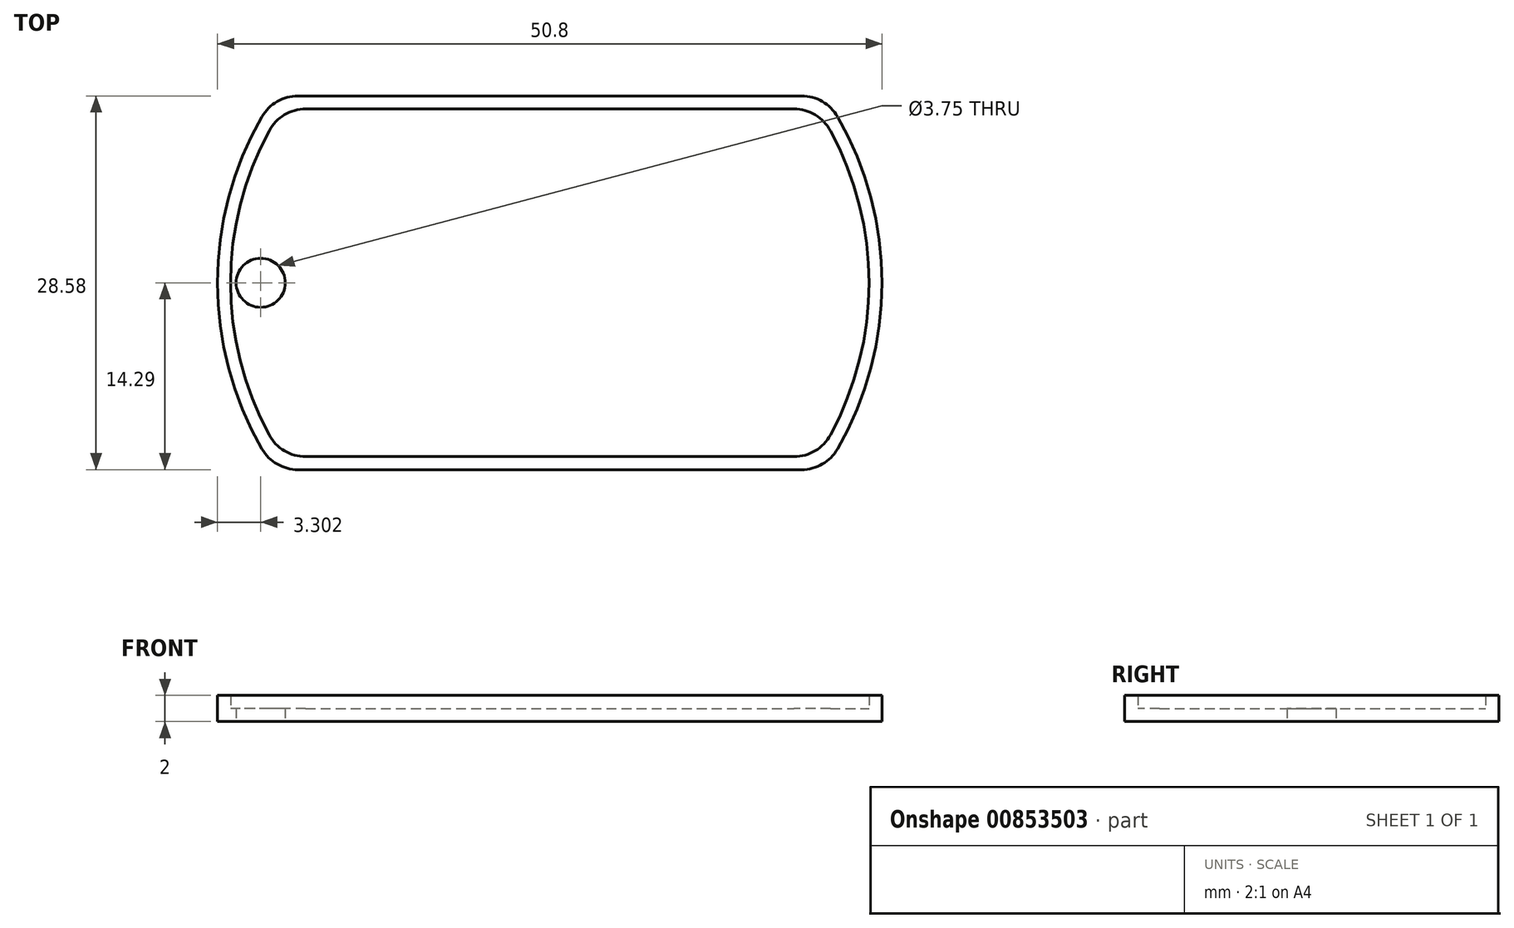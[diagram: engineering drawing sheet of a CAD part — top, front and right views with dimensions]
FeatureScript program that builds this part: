
annotation { "Feature Type Name" : "Feature", "Feature Type Description" : "" }
export const myFeature = defineFeature(function(context is Context, id is Id, definition is map)
    precondition{}
    {
        {
            var Q0;
            Q0=qCreatedBy(makeId("Top.planeOp"),FACE);
            var sketch = newSketch(context, id + "F0", { "sketchPlane" : qUnion([Q0])});
            skArc(sketch, "E0", {"start": v(-22, 12.7) * mm, "mid": v(-25.4, 0) * mm, "end": v(-22, -12.7) * mm});
            skLineSegment(sketch, "E1.top", {"start": v(-19.25, -14.29) * mm, "end": v(19.25, -14.29) * mm});
            skArc(sketch, "E2.trimOffspring", {"start": v(22, -12.7) * mm, "mid": v(25.4, 0) * mm, "end": v(22, 12.7) * mm});
            skLineSegment(sketch, "E3", {"start": v(-19.25, 14.29) * mm, "end": v(19.25, 14.29) * mm});
            skPoint(sketch, "E4.visualSharp", {"position": v(-21, 14.29) * mm});
            skArc(sketch, "E4.filletArc", {"start": v(-19.25, 14.29) * mm, "mid": v(-20.83, 13.86) * mm, "end": v(-22, 12.7) * mm});
            skPoint(sketch, "E5.visualSharp", {"position": v(21, 14.29) * mm});
            skArc(sketch, "E5.filletArc", {"start": v(22, 12.7) * mm, "mid": v(20.83, 13.86) * mm, "end": v(19.25, 14.29) * mm});
            skPoint(sketch, "E6.visualSharp", {"position": v(21, -14.29) * mm});
            skArc(sketch, "E6.filletArc", {"start": v(19.25, -14.29) * mm, "mid": v(20.83, -13.86) * mm, "end": v(22, -12.7) * mm});
            skPoint(sketch, "E7.visualSharp", {"position": v(-21, -14.29) * mm});
            skArc(sketch, "E7.filletArc", {"start": v(-22, -12.7) * mm, "mid": v(-20.83, -13.86) * mm, "end": v(-19.25, -14.29) * mm});
            skCircle(sketch, "E8", {"center": v(-22.1, 0) * mm, "radius": 1.87 * mm});
            skSolve(sketch);
        }
        {
            var Q0;
            Q0=makeQuery(id+"F0.imprint","IMPRINT",FACE,{"disambiguationData":[TD([[makeQuery(id+"F0.imprint","IMPRINT",EDGE,{"derivedFrom":sQuery(id+"F0.wireOp",EDGE,"E0")}),1.0]])]});
            extrude(context, id + "F1", {"entities" : qUnion([Q0]), "depth" : 1 * mm, "offsetDistance" : 25.4 * mm});
        }
        {
            var Q0;
            Q0=makeQuery(id+"F1.opExtrude","CAP_FACE",FACE,{"disambiguationData":[OSD([sQuery(id+"F0.wireOp",EDGE,"E0"),sQuery(id+"F0.wireOp",EDGE,"E1.top"),sQuery(id+"F0.wireOp",EDGE,"E2.trimOffspring"),sQuery(id+"F0.wireOp",EDGE,"E3"),sQuery(id+"F0.wireOp",EDGE,"E4.filletArc"),sQuery(id+"F0.wireOp",EDGE,"E5.filletArc"),sQuery(id+"F0.wireOp",EDGE,"E6.filletArc"),sQuery(id+"F0.wireOp",EDGE,"E7.filletArc")])],"isStart":false});
            var sketch = newSketch(context, id + "F2", { "sketchPlane" : qUnion([Q0])});
            skLineSegment(sketch, "E9.0", {"start": v(-18.66, 13.29) * mm, "end": v(18.66, 13.29) * mm});
            skArc(sketch, "E9.1", {"start": v(-21.45, 11.63) * mm, "mid": v(-24.4, 0) * mm, "end": v(-21.45, -11.63) * mm});
            skLineSegment(sketch, "E9.2", {"start": v(-18.66, -13.29) * mm, "end": v(18.66, -13.29) * mm});
            skArc(sketch, "E9.3", {"start": v(21.45, -11.63) * mm, "mid": v(24.4, 0) * mm, "end": v(21.45, 11.63) * mm});
            skPoint(sketch, "E10.visualSharp", {"position": v(-20.46, 13.29) * mm});
            skArc(sketch, "E10.filletArc", {"start": v(-18.66, 13.29) * mm, "mid": v(-20.29, 12.84) * mm, "end": v(-21.45, 11.63) * mm});
            skPoint(sketch, "E11.visualSharp", {"position": v(20.46, 13.29) * mm});
            skArc(sketch, "E11.filletArc", {"start": v(21.45, 11.63) * mm, "mid": v(20.29, 12.84) * mm, "end": v(18.66, 13.29) * mm});
            skPoint(sketch, "E12.visualSharp", {"position": v(20.46, -13.29) * mm});
            skArc(sketch, "E12.filletArc", {"start": v(18.66, -13.29) * mm, "mid": v(20.29, -12.84) * mm, "end": v(21.45, -11.63) * mm});
            skPoint(sketch, "E13.visualSharp", {"position": v(-20.46, -13.29) * mm});
            skArc(sketch, "E13.filletArc", {"start": v(-21.45, -11.63) * mm, "mid": v(-20.29, -12.84) * mm, "end": v(-18.66, -13.29) * mm});
            skLineSegment(sketch, "E14.0", {"start": v(-19.25, 14.29) * mm, "end": v(19.25, 14.29) * mm});
            skArc(sketch, "E14.1", {"start": v(-22, 12.7) * mm, "mid": v(-25.4, 0) * mm, "end": v(-22, -12.7) * mm});
            skLineSegment(sketch, "E14.2", {"start": v(-19.25, -14.29) * mm, "end": v(19.25, -14.29) * mm});
            skArc(sketch, "E14.3", {"start": v(22, -12.7) * mm, "mid": v(25.4, 0) * mm, "end": v(22, 12.7) * mm});
            skPoint(sketch, "E15.visualSharp", {"position": v(-21, -14.29) * mm});
            skArc(sketch, "E15.filletArc", {"start": v(-22, -12.7) * mm, "mid": v(-20.83, -13.86) * mm, "end": v(-19.25, -14.29) * mm});
            skPoint(sketch, "E16.visualSharp", {"position": v(21, -14.29) * mm});
            skArc(sketch, "E16.filletArc", {"start": v(19.25, -14.29) * mm, "mid": v(20.83, -13.86) * mm, "end": v(22, -12.7) * mm});
            skPoint(sketch, "E17.visualSharp", {"position": v(21, 14.29) * mm});
            skArc(sketch, "E17.filletArc", {"start": v(22, 12.7) * mm, "mid": v(20.83, 13.86) * mm, "end": v(19.25, 14.29) * mm});
            skPoint(sketch, "E18.visualSharp", {"position": v(-21, 14.29) * mm});
            skArc(sketch, "E18.filletArc", {"start": v(-19.25, 14.29) * mm, "mid": v(-20.83, 13.86) * mm, "end": v(-22, 12.7) * mm});
            skSolve(sketch);
        }
        {
            var Q0;
            Q0=makeQuery(id+"F2.imprint","IMPRINT",FACE,{"disambiguationData":[TD([[makeQuery(id+"F2.imprint","IMPRINT",EDGE,{"derivedFrom":sQuery(id+"F2.wireOp",EDGE,"E9.0")}),1.0]])]});
            extrude(context, id + "F3", {"entities" : qUnion([Q0]), "operationType" : NewBodyOperationType.ADD, "depth" : 1 * mm, "offsetDistance" : 25.4 * mm});
        }
        {
            var Q0;
            Q0=makeQuery(id+"F1.opExtrude","CAP_FACE",FACE,{"disambiguationData":[OSD([sQuery(id+"F0.wireOp",EDGE,"E0"),sQuery(id+"F0.wireOp",EDGE,"E1.top"),sQuery(id+"F0.wireOp",EDGE,"E2.trimOffspring"),sQuery(id+"F0.wireOp",EDGE,"E3"),sQuery(id+"F0.wireOp",EDGE,"E4.filletArc"),sQuery(id+"F0.wireOp",EDGE,"E5.filletArc"),sQuery(id+"F0.wireOp",EDGE,"E6.filletArc"),sQuery(id+"F0.wireOp",EDGE,"E7.filletArc"),sQuery(id+"F0.wireOp",EDGE,"E8")])],"isStart":false});
            var sketch = newSketch(context, id + "F4", { "sketchPlane" : qUnion([Q0])});
            skText(sketch, "E19", { "text": "skyler \n tepp", "fontName": "RobotoSlab-Regular.ttf"});
            const initialGuessF4  = {"E19": [-0.00388, 0.00292, 1, 0, 0.00595]};
            skSetInitialGuess(sketch, initialGuessF4);
            skSolve(sketch);
        }
        {
            var Q0;
            Q0 = qConstructionFilter(qBodyType(qCreatedBy(id + "F4" ,EDGE), BodyType.WIRE), ConstructionObject.NO);
            extrude(context, id + "F5", {"bodyType" : ToolBodyType.SURFACE, "surfaceEntities" : qUnion([Q0]), "endBound" : BoundingType.SYMMETRIC, "depth" : 1.27 * mm, "offsetDistance" : 25.4 * mm});
        }
    });
